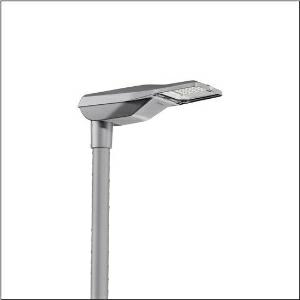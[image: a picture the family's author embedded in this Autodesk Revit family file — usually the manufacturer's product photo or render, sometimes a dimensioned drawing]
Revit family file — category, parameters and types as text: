
# Revit family: streetlight_sl_21_iq_micro___p0_8a_5xe1u31d08db_7b75
name_source: partatom
category: Lighting Fixtures
units: mm (PartAtom-declared; Revit-internal decimal feet)

## family parameters
Cut with Voids When Loaded = No
Host = Face
Light Source = No
Part Type = Normal
Room Calculation Point = No
Round Connector Dimension = Use Diameter
Shared = No

## types (1)
- --- (1 x LED, 4750 lm, 36.4 W, 3000K)
    Apparent Load = 36 VA
    CIE Flux Codes = 33 69 96 100 100
    Color Rendering = 70
    Color Temperature = 3000K
    Default Elevation = 1800 mm
    Description = Streetlight SL 21 iQ micro, mast luminaire, primary light control with lens, of PMMA, primary optical cover: cover, of toughened safety glass, transparent, light distribution: P0.8a, light emission: direct distribution, primary light characteristic: asymmetric, installation type: post-top, side-entry, LED, High Power LED, rated luminous flux: 4.750lm, luminous efficacy: 131lm/W, light colour: 730, colour temperature: 3000K, control gear: iQ-Comfort, control: pre-setting: linear dimming characteristic, Auto-Match, Temp-Guard, Lumen-Switch, Night-Set, Smart-Wire, Light-Fading, Desk-Remote (wireless, voltage-free reading and setting of iQ features in the workshop via application-optimized NFC function/RFID function), optimised constant luminous flux control (CLO 2.0), mains connection: 220..240V, AC, 50/60Hz, start of lifetime: 36W, end of service life: 38W, reduction: 16W, luminaire housing, of diecast aluminium, powder-coated, Siteco® metallic grey (DB 702S), corrosivity category C5 mid according to DIN EN ISO 12944, please order mast flange separately, inclination adjustable: 0°, 5°, 10°, 15°, sealing non-destructively replaceable, multi-level sealing system, length: 528mm, width: 235mm, height: 110mm, mast flange for spigot size: 42mm (side-entry): 5XC10008XM4, 60/48mm (side-entry/post-top): 5XC10108XM2, 76/60mm (side-entry/post-top): 5XC10108XM1, protection rating (complete): IP66, insulation class (complete): insulation class II (safety insulation), certification: CE, ENEC, ENEC+, VDE, impact resistance: IK10, permissible operating ambient temperature for outdoor applications: -40..+50°C, standard-compliant lighting for roads and squares, packaging unit: 1 piece

Light Distribution: P0.8a
    Height = 110 mm
    Lamp = 1 x LED
    Lamp Light Flux = 4750 lm
    Lamp Power = 36.4 W
    Lamp count = 1
    Length = 528 mm
    Luminous efficacy = 130 lm/W
    Manufacturer = Siteco
    ModVariant = No
    Model = 5XE1U31D08DB
    Number of Poles = 1
    OnlyDefault = Yes
    Power Factor = 1
    Product Name = Streetlight SL 21 iQ micro | P0.8a
    Product group = mast luminaire | pylon top
    ProductGroupID = 6100
    Protection Class = Protection class II
    Protection Degree = IP 66
    RLX_Detail_Level = 1
    RLX_Emergency_Light_Flux = 0 lm
    RLX_Emergency_Type = 0
    RLX_Emergency_Type_DB = No
    RlxData = <blob elided: 99573 chars, md5=8ba75b95>
    Socket = socket
    Standby Power = 0 W
    System Light Flux = 4750 lm
    System Power = 36 W
    Type Comments = factory setting: luminous flux: 100 % | dim-lin: 254 | 715 mA
    Type Image = l_1006881.jpg
    URL = http://relux.com
    VarID = @adj_073114
    Voltage = 0 V
    Weight = 0.00 kg
    Width = 235 mm

## geometry (parser evidence)
native form markers: Blend x4, Sweep x8
no freeform markers — native parametric forms only
